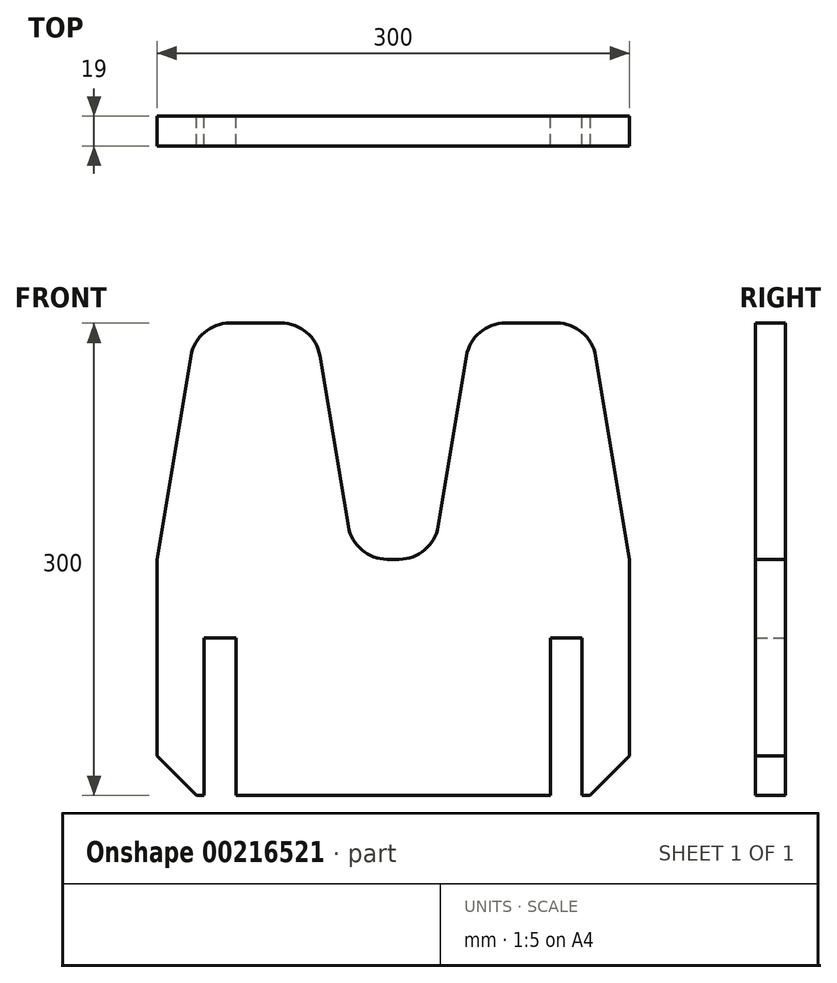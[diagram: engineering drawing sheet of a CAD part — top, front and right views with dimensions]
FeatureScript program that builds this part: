
annotation { "Feature Type Name" : "Feature", "Feature Type Description" : "" }
export const myFeature = defineFeature(function(context is Context, id is Id, definition is map)
    precondition{}
    {
        {
            var Q0;
            Q0=qCreatedBy(makeId("Front.planeOp"),FACE);
            var sketch = newSketch(context, id + "F0", { "sketchPlane" : qUnion([Q0])});
            skLineSegment(sketch, "E0.bottom", {"start": v(-150, 150) * mm, "end": v(150, 150) * mm, "construction": true});
            skLineSegment(sketch, "E0.left", {"start": v(-150, 150) * mm, "end": v(-150, -150) * mm});
            skLineSegment(sketch, "E0.right", {"start": v(150, 150) * mm, "end": v(150, -150) * mm});
            skLineSegment(sketch, "E1.top", {"start": v(-120, -50) * mm, "end": v(-100, -50) * mm});
            skLineSegment(sketch, "E1.left", {"start": v(-120, -150) * mm, "end": v(-120, -50) * mm});
            skLineSegment(sketch, "E1.right", {"start": v(-100, -150) * mm, "end": v(-100, -50) * mm});
            skLineSegment(sketch, "E2", {"start": v(0, 150) * mm, "end": v(0, -150) * mm, "construction": true});
            skLineSegment(sketch, "E3.MirrorCS", {"start": v(120, -150) * mm, "end": v(120, -50) * mm});
            skLineSegment(sketch, "E4.MirrorCS", {"start": v(120, -50) * mm, "end": v(100, -50) * mm});
            skLineSegment(sketch, "E5.MirrorCS", {"start": v(100, -150) * mm, "end": v(100, -50) * mm});
            skLineSegment(sketch, "E6.trimOffspring", {"start": v(120, -150) * mm, "end": v(150, -150) * mm});
            skLineSegment(sketch, "E7.trimOffspring", {"start": v(-100, -150) * mm, "end": v(0, -150) * mm});
            skLineSegment(sketch, "E8", {"start": v(-150, -150) * mm, "end": v(-120, -150) * mm});
            skLineSegment(sketch, "E9", {"start": v(0, -150) * mm, "end": v(100, -150) * mm});
            skLineSegment(sketch, "E10", {"start": v(-50, 150) * mm, "end": v(-25, 0) * mm});
            skLineSegment(sketch, "E11", {"start": v(-25, 0) * mm, "end": v(0, 0) * mm});
            skLineSegment(sketch, "E12", {"start": v(-150, 150) * mm, "end": v(-50, 150) * mm});
            skLineSegment(sketch, "E13.MirrorCS", {"start": v(50, 150) * mm, "end": v(25, 0) * mm});
            skLineSegment(sketch, "E14.MirrorCS", {"start": v(25, 0) * mm, "end": v(0, 0) * mm});
            skLineSegment(sketch, "E15.MirrorCS", {"start": v(150, 150) * mm, "end": v(50, 150) * mm});
            skSolve(sketch);
        }
        {
            var Q0;
            Q0=makeQuery(id+"F0.imprint","IMPRINT",FACE,{"disambiguationData":[TD([[makeQuery(id+"F0.imprint","IMPRINT",EDGE,{"derivedFrom":sQuery(id+"F0.wireOp",EDGE,"E0.left")}),1.0]])]});
            extrude(context, id + "F1", {"entities" : qUnion([Q0]), "depth" : 19 * mm, "symmetric" : true});
        }
        {
            var Q0;
            Q0=makeQuery(id+"F1.opExtrude","SWEPT_EDGE",EDGE,{"disambiguationData":[OSD([sQuery(id+"F0.wireOp",EDGE,"E0.right"),sQuery(id+"F0.wireOp",EDGE,"E15.MirrorCS")])]});
            chamfer(context, id + "F2", {"entities" : qUnion([Q0]), "chamferType" : ChamferType.TWO_OFFSETS, "width1" : 25 * mm, "oppositeDirection" : false, "width2" : 150 * mm, "tangentPropagation" : true});
        }
        {
            var Q0;
            Q0=makeQuery(id+"F1.opExtrude","SWEPT_EDGE",EDGE,{"disambiguationData":[OSD([sQuery(id+"F0.wireOp",EDGE,"E0.left"),sQuery(id+"F0.wireOp",EDGE,"E12")])]});
            chamfer(context, id + "F3", {"entities" : qUnion([Q0]), "chamferType" : ChamferType.TWO_OFFSETS, "width1" : 25 * mm, "oppositeDirection" : true, "width2" : 150 * mm, "tangentPropagation" : true});
        }
        {
            var Q0;
            {var subQ0=sQuery(id+"F0.wireOp",EDGE,"E12");Q0=makeQuery(id+"F3.opChamfer","BLEND_EDGE",EDGE,{"blendedFrom":[makeQuery(id+"F1.opExtrude","SWEPT_EDGE",EDGE,{"disambiguationData":[OSD([sQuery(id+"F0.wireOp",EDGE,"E0.left"),subQ0])]}),makeQuery(id+"F1.opExtrude","SWEPT_FACE",FACE,{"disambiguationData":[OSD([subQ0])]})],"blendedInto":[makeQuery(id+"F1.opExtrude","SWEPT_FACE",FACE,{"disambiguationData":[OSD([subQ0])]})]});}
            var Q1;
            Q1=makeQuery(id+"F1.opExtrude","SWEPT_EDGE",EDGE,{"disambiguationData":[OSD([sQuery(id+"F0.wireOp",EDGE,"E10"),sQuery(id+"F0.wireOp",EDGE,"E12")])]});
            var Q2;
            Q2=makeQuery(id+"F1.opExtrude","SWEPT_EDGE",EDGE,{"disambiguationData":[OSD([sQuery(id+"F0.wireOp",EDGE,"E13.MirrorCS"),sQuery(id+"F0.wireOp",EDGE,"E15.MirrorCS")])]});
            var Q3;
            {var subQ0=sQuery(id+"F0.wireOp",EDGE,"E15.MirrorCS");Q3=makeQuery(id+"F2.opChamfer","BLEND_EDGE",EDGE,{"blendedFrom":[makeQuery(id+"F1.opExtrude","SWEPT_EDGE",EDGE,{"disambiguationData":[OSD([sQuery(id+"F0.wireOp",EDGE,"E0.right"),subQ0])]}),makeQuery(id+"F1.opExtrude","SWEPT_FACE",FACE,{"disambiguationData":[OSD([subQ0])]})],"blendedInto":[makeQuery(id+"F1.opExtrude","SWEPT_FACE",FACE,{"disambiguationData":[OSD([subQ0])]})]});}
            var Q4;
            Q4=makeQuery(id+"F1.opExtrude","SWEPT_EDGE",EDGE,{"disambiguationData":[OSD([sQuery(id+"F0.wireOp",EDGE,"E13.MirrorCS"),sQuery(id+"F0.wireOp",EDGE,"E14.MirrorCS")])]});
            var Q5;
            Q5=makeQuery(id+"F1.opExtrude","SWEPT_EDGE",EDGE,{"disambiguationData":[OSD([sQuery(id+"F0.wireOp",EDGE,"E10"),sQuery(id+"F0.wireOp",EDGE,"E11")])]});
            fillet(context, id + "F4", {"entities" : qUnion([Q0, Q1, Q2, Q3, Q4, Q5]), "radius" : 25 * mm, "tangentPropagation" : true, "allowEdgeOverflow" : false});
        }
        {
            var Q0;
            Q0=makeQuery(id+"F1.opExtrude","SWEPT_EDGE",EDGE,{"disambiguationData":[OSD([sQuery(id+"F0.wireOp",EDGE,"E0.left"),sQuery(id+"F0.wireOp",EDGE,"E8")])]});
            var Q1;
            Q1=makeQuery(id+"F1.opExtrude","SWEPT_EDGE",EDGE,{"disambiguationData":[OSD([sQuery(id+"F0.wireOp",EDGE,"E0.right"),sQuery(id+"F0.wireOp",EDGE,"E6.trimOffspring")])]});
            chamfer(context, id + "F5", {"entities" : qUnion([Q0, Q1]), "width" : 25 * mm, "tangentPropagation" : true});
        }
    });
